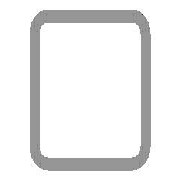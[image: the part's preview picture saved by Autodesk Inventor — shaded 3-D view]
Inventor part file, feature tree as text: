
AUTODESK INVENTOR PART (.ipt)
format: ipt  version: 2025 (Build 290162010, 162A)  size: 148,992 bytes
history: native  units: mm (DEFAULTED — no unit token found)
features: other x3, sketch x2, projected_geometry x2, extrude x1, plane x1
ambient origin geometry x8: Origin, YZ Plane, XZ Plane, XY Plane, X Axis, Y Axis, Z Axis, Center Point
bodies: Solid1 (feature_tree), Body (feature_tree)
feature tree (9):
  other  "Driven Length"
  other  "Start plane"
  other  "End plane"
  extrude  "Extrusion2"  TaperAngle=0.0deg  [1 undecoded]
  sketch  "Sketch3"  dims[d3=5000.0mm d4=0.0mm]
  plane  "Work Plane3"
  sketch  "Sketch5"  dims[d7=8.0mm d9=120.0mm d11=120.0mm d12=4.0mm d13=-0.0mm d14=5000.0mm d15=60.0mm d16=60.0mm d17=90.0deg d18=5000.0mm d19=15.0deg d20=0.0mm d21=0.0mm]
  projected_geometry  "Projected Loop1"
  projected_geometry  "Projected Loop2"
note: 1 required parameter value undecoded (feature->parameter linkage not recoverable at this tier; creation-order binding heuristic only, values carry confidence <= 0.55)
